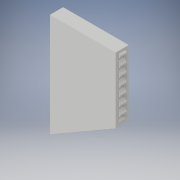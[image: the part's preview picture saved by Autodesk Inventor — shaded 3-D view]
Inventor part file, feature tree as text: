
AUTODESK INVENTOR PART (.ipt)
format: ipt  version: 2017 (Build 210142000, 142)  size: 342,016 bytes
history: native  units: in
note: dims shown in document units (in); Inventor stores cm internally (conversion verified against a paired STEP export)
features: extrude x3, sketch x1
ambient origin geometry x8: Origin, YZ Plane, XZ Plane, XY Plane, X Axis, Y Axis, Z Axis, Center Point
bodies: Solid1 (feature_tree)
feature tree (4):
  extrude  "door"  Depth=1.0in
  sketch  "Sketch3"  dims[d143=10.0in d144=0.0in d282=1.0in d283=1.0in d284=1.5in d285=1.5in d350=1.5in d351=1.0in d352=1.5in d353=0.9496in d356=0.9496in d358=1.0in d359=1.0in d360=1.0in d361=1.5in d362=1.5in d363=1.5in d364=1.0in d365=1.5in d366=0.9496in d367=0.9496in d368=1.0in d369=1.0in d370=1.0in d371=1.5in d372=1.5in d373=1.5in d374=1.0in d375=1.5in d376=0.9496in d377=0.9496in d378=1.0in d379=1.0in d380=1.0in d381=1.5in d382=1.5in d383=1.5in d384=1.0in d385=1.5in d386=0.9496in d387=0.9496in d388=1.0in d389=1.0in d390=1.0in d391=1.5in d392=1.5in d393=1.5in d394=1.0in d395=1.5in d396=0.9496in d397=0.9496in d398=1.0in d399=1.0in d400=1.0in d401=1.5in d402=1.5in d403=1.5in d404=1.0in d405=1.5in d406=0.9496in d407=0.9496in d408=1.0in d409=1.0in d410=1.0in d411=1.5in d412=1.5in d413=1.5in d414=1.0in d415=1.5in d416=0.9496in d417=0.9496in d418=1.0in d419=1.0in d420=1.0in d421=1.5in d422=1.5in d423=1.5in d424=1.0in d425=1.5in d426=0.9496in d427=0.9496in d428=1.0in d429=1.0in d430=1.0in d431=1.5in d432=1.5in d436=0.9496in d439=5.0in d440=0.0in d441=5.0in d442=0.0in d446=78.8675in]
  extrude  "connection give"  Depth=5.0in
  extrude  "connection receive"  Depth=1.0in
